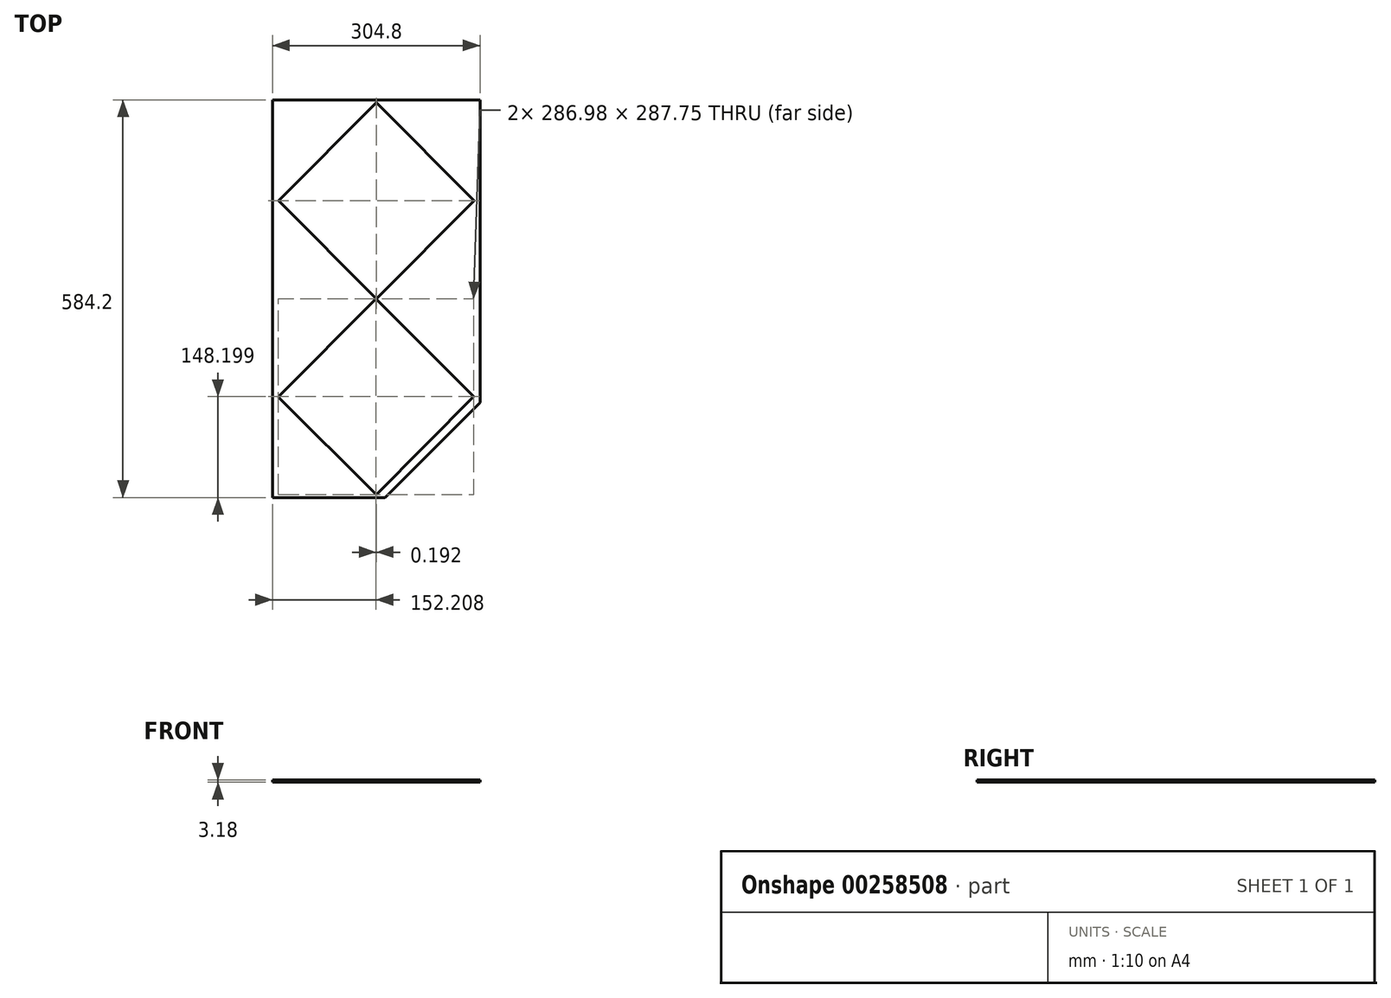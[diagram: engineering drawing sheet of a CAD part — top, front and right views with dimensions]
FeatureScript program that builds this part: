
annotation { "Feature Type Name" : "Feature", "Feature Type Description" : "" }
export const myFeature = defineFeature(function(context is Context, id is Id, definition is map)
    precondition{}
    {
        {
            var Q0;
            Q0=qCreatedBy(makeId("Top.planeOp"),FACE);
            var sketch = newSketch(context, id + "F0", { "sketchPlane" : qUnion([Q0])});
            skLineSegment(sketch, "E0.bottom", {"start": v(152.4, 292.1) * mm, "end": v(-152.4, 292.1) * mm});
            skLineSegment(sketch, "E0.top", {"start": v(12.7, -292.1) * mm, "end": v(-152.4, -292.1) * mm});
            skLineSegment(sketch, "E0.left", {"start": v(152.4, 292.1) * mm, "end": v(152.4, -152.4) * mm});
            skLineSegment(sketch, "E0.right", {"start": v(-152.4, 292.1) * mm, "end": v(-152.4, -292.1) * mm});
            skPoint(sketch, "E0.middle", {"position": v(0, 0) * mm});
            skLineSegment(sketch, "E1", {"start": v(12.7, -292.1) * mm, "end": v(152.4, -152.4) * mm});
            skPoint(sketch, "E2.orphan", {"position": v(152.4, -292.1) * mm});
            skSolve(sketch);
        }
        {
            var Q0;
            Q0 = qSketchRegion(id + "F0", true);
            extrude(context, id + "F1", {"entities" : qUnion([Q0]), "depth" : 3.17 * mm});
        }
        {
            var Q0;
            Q0=makeQuery(id+"F1.opExtrude","CAP_FACE",FACE,{"disambiguationData":[OSD([sQuery(id+"F0.wireOp",EDGE,"E0.bottom"),sQuery(id+"F0.wireOp",EDGE,"E0.top"),sQuery(id+"F0.wireOp",EDGE,"E0.left"),sQuery(id+"F0.wireOp",EDGE,"E0.right"),sQuery(id+"F0.wireOp",EDGE,"E1")])],"isStart":false});
            var sketch = newSketch(context, id + "F2", { "sketchPlane" : qUnion([Q0])});
            skPoint(sketch, "E3.end.orphan", {"position": v(0, 0) * mm});
            skPoint(sketch, "E4.visualSharp", {"position": v(0, 287.78) * mm});
            skPoint(sketch, "E5.visualSharp", {"position": v(-143.5, 143.9) * mm});
            skPoint(sketch, "E6.visualSharp", {"position": v(143.5, 143.9) * mm});
            skPoint(sketch, "E7.visualSharp", {"position": v(0, 0.03) * mm});
            skPoint(sketch, "E8.visualSharp", {"position": v(-0.38, -0.03) * mm});
            skPoint(sketch, "E9.visualSharp", {"position": v(-143.68, -144.1) * mm});
            skPoint(sketch, "E10.visualSharp", {"position": v(143.3, -143.7) * mm});
            skPoint(sketch, "E11.visualSharp", {"position": v(0, -287.78) * mm});
            skLineSegment(sketch, "E12", {"start": v(0, 292.1) * mm, "end": v(0, -292.1) * mm});
            skLineSegment(sketch, "E13", {"start": v(-143.5, 143.9) * mm, "end": v(143.5, 143.9) * mm, "construction": true});
            skPoint(sketch, "E14", {"position": v(0, 143.9) * mm});
            skLineSegment(sketch, "E15", {"start": v(0, 0.03) * mm, "end": v(-143.5, 143.9) * mm});
            skLineSegment(sketch, "E16", {"start": v(0, 0.03) * mm, "end": v(143.5, 143.9) * mm});
            skLineSegment(sketch, "E17", {"start": v(143.5, 143.9) * mm, "end": v(0, 287.78) * mm});
            skLineSegment(sketch, "E18", {"start": v(0, 287.78) * mm, "end": v(-143.5, 143.9) * mm});
            skLineSegment(sketch, "E19", {"start": v(0, -287.78) * mm, "end": v(-143.68, -144.1) * mm});
            skLineSegment(sketch, "E20", {"start": v(-143.68, -144.1) * mm, "end": v(-0.38, -0.03) * mm});
            skLineSegment(sketch, "E21", {"start": v(-0.38, -0.03) * mm, "end": v(143.3, -143.7) * mm});
            skLineSegment(sketch, "E22", {"start": v(0, -287.78) * mm, "end": v(143.3, -143.7) * mm});
            skSolve(sketch);
        }
        {
            var Q0;
            Q0 = qSketchRegion(id + "F2", true);
            extrude(context, id + "F3", {"entities" : qUnion([Q0]), "operationType" : NewBodyOperationType.REMOVE, "oppositeDirection" : true, "depth" : 25.4 * mm});
        }
    });
